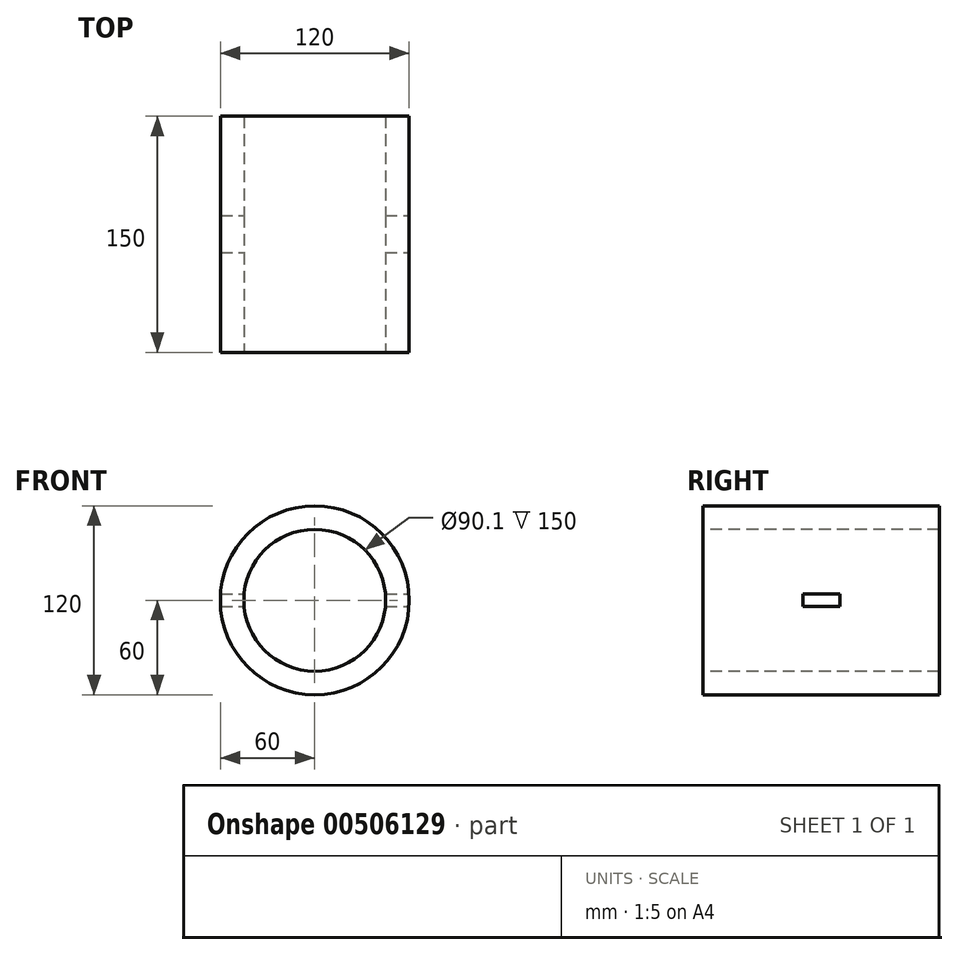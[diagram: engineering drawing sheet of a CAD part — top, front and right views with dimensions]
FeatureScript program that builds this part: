
annotation { "Feature Type Name" : "Feature", "Feature Type Description" : "" }
export const myFeature = defineFeature(function(context is Context, id is Id, definition is map)
    precondition{}
    {
        {
            var Q0;
            Q0=qCreatedBy(makeId("Front.planeOp"),FACE);
            var sketch = newSketch(context, id + "F0", { "sketchPlane" : qUnion([Q0])});
            skCircle(sketch, "E0", {"center": v(0, 0) * mm, "radius": 60 * mm});
            skSolve(sketch);
        }
        {
            var Q0;
            Q0=makeQuery(id+"F0.imprint","IMPRINT",FACE,{"disambiguationData":[TD([[makeQuery(id+"F0.imprint","IMPRINT",EDGE,{"derivedFrom":sQuery(id+"F0.wireOp",EDGE,"E0")}),1.0]])]});
            extrude(context, id + "F1", {"entities" : qUnion([Q0]), "endBound" : BoundingType.SYMMETRIC, "depth" : 150 * mm});
        }
        {
            var Q0;
            Q0=makeQuery(id+"F1.opExtrude","CAP_FACE",FACE,{"disambiguationData":[OSD([sQuery(id+"F0.wireOp",EDGE,"E0")])],"isStart":false});
            var sketch = newSketch(context, id + "F2", { "sketchPlane" : qUnion([Q0])});
            skCircle(sketch, "E1", {"center": v(0, 0) * mm, "radius": 45.05 * mm});
            skSolve(sketch);
        }
        {
            var Q0;
            Q0=makeQuery(id+"F2.imprint","IMPRINT",FACE,{"disambiguationData":[TD([[makeQuery(id+"F2.imprint","IMPRINT",EDGE,{"derivedFrom":sQuery(id+"F2.wireOp",EDGE,"E1")}),1.0]])]});
            extrude(context, id + "F3", {"entities" : qUnion([Q0]), "operationType" : NewBodyOperationType.REMOVE, "oppositeDirection" : true, "depth" : 300 * mm});
        }
        {
            var Q0;
            Q0=qCreatedBy(makeId("Right.planeOp"),FACE);
            var sketch = newSketch(context, id + "F4", { "sketchPlane" : qUnion([Q0])});
            skLineSegment(sketch, "E2.bottom", {"start": v(-11.75, -3.9) * mm, "end": v(11.75, -3.9) * mm});
            skLineSegment(sketch, "E2.top", {"start": v(-11.75, 3.9) * mm, "end": v(11.75, 3.9) * mm});
            skLineSegment(sketch, "E2.left", {"start": v(-11.75, -3.9) * mm, "end": v(-11.75, 3.9) * mm});
            skLineSegment(sketch, "E2.right", {"start": v(11.75, -3.9) * mm, "end": v(11.75, 3.9) * mm});
            skPoint(sketch, "E2.middle", {"position": v(0, 0) * mm});
            skSolve(sketch);
        }
        {
            var Q0;
            Q0=makeQuery(id+"F4.imprint","IMPRINT",FACE,{"disambiguationData":[TD([[makeQuery(id+"F4.imprint","IMPRINT",EDGE,{"derivedFrom":sQuery(id+"F4.wireOp",EDGE,"E2.bottom")}),1.0]])]});
            extrude(context, id + "F5", {"entities" : qUnion([Q0]), "operationType" : NewBodyOperationType.REMOVE, "endBound" : BoundingType.SYMMETRIC, "oppositeDirection" : true, "depth" : 157.8 * mm});
        }
    });
